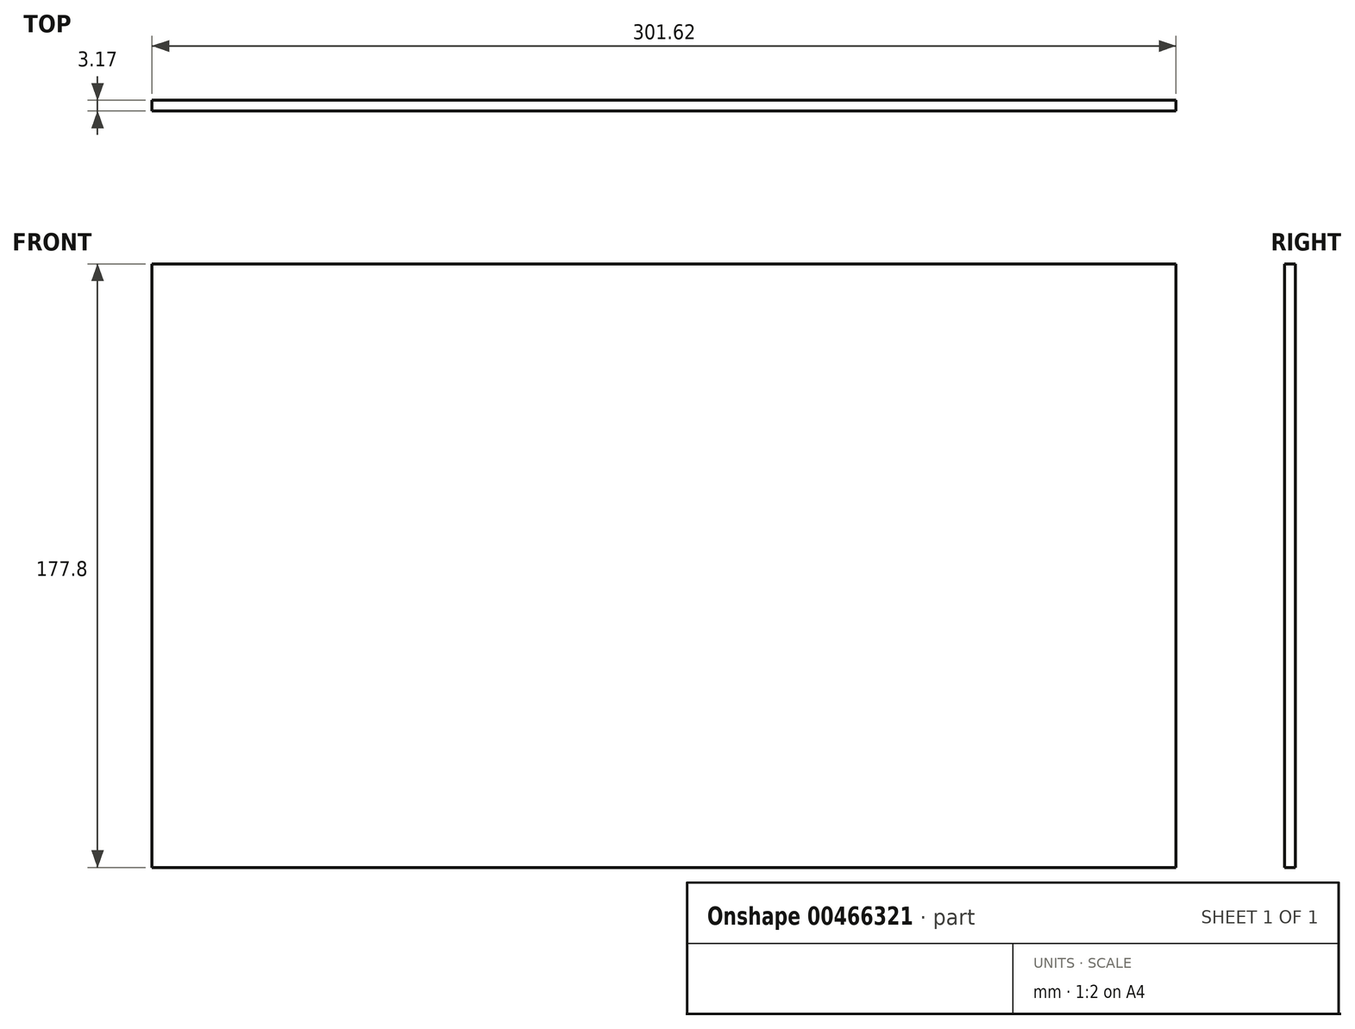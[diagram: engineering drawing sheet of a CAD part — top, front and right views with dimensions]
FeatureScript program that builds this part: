
annotation { "Feature Type Name" : "Feature", "Feature Type Description" : "" }
export const myFeature = defineFeature(function(context is Context, id is Id, definition is map)
    precondition{}
    {
        {
            var Q0;
            Q0=qCreatedBy(makeId("Front.planeOp"),FACE);
            var sketch = newSketch(context, id + "F0", { "sketchPlane" : qUnion([Q0])});
            skLineSegment(sketch, "E0.bottom", {"start": v(-146.21, 82.4) * mm, "end": v(155.41, 82.4) * mm});
            skLineSegment(sketch, "E0.top", {"start": v(-146.21, -95.4) * mm, "end": v(155.41, -95.4) * mm});
            skLineSegment(sketch, "E0.left", {"start": v(-146.21, 82.4) * mm, "end": v(-146.21, -95.4) * mm});
            skLineSegment(sketch, "E0.right", {"start": v(155.41, 82.4) * mm, "end": v(155.41, -95.4) * mm});
            skSolve(sketch);
        }
        {
            var Q0;
            Q0=makeQuery(id+"F0.imprint","IMPRINT",FACE,{"disambiguationData":[TD([[makeQuery(id+"F0.imprint","IMPRINT",EDGE,{"derivedFrom":sQuery(id+"F0.wireOp",EDGE,"E0.bottom")}),-1.0]])]});
            extrude(context, id + "F1", {"entities" : qUnion([Q0]), "depth" : 3.17 * mm});
        }
    });
